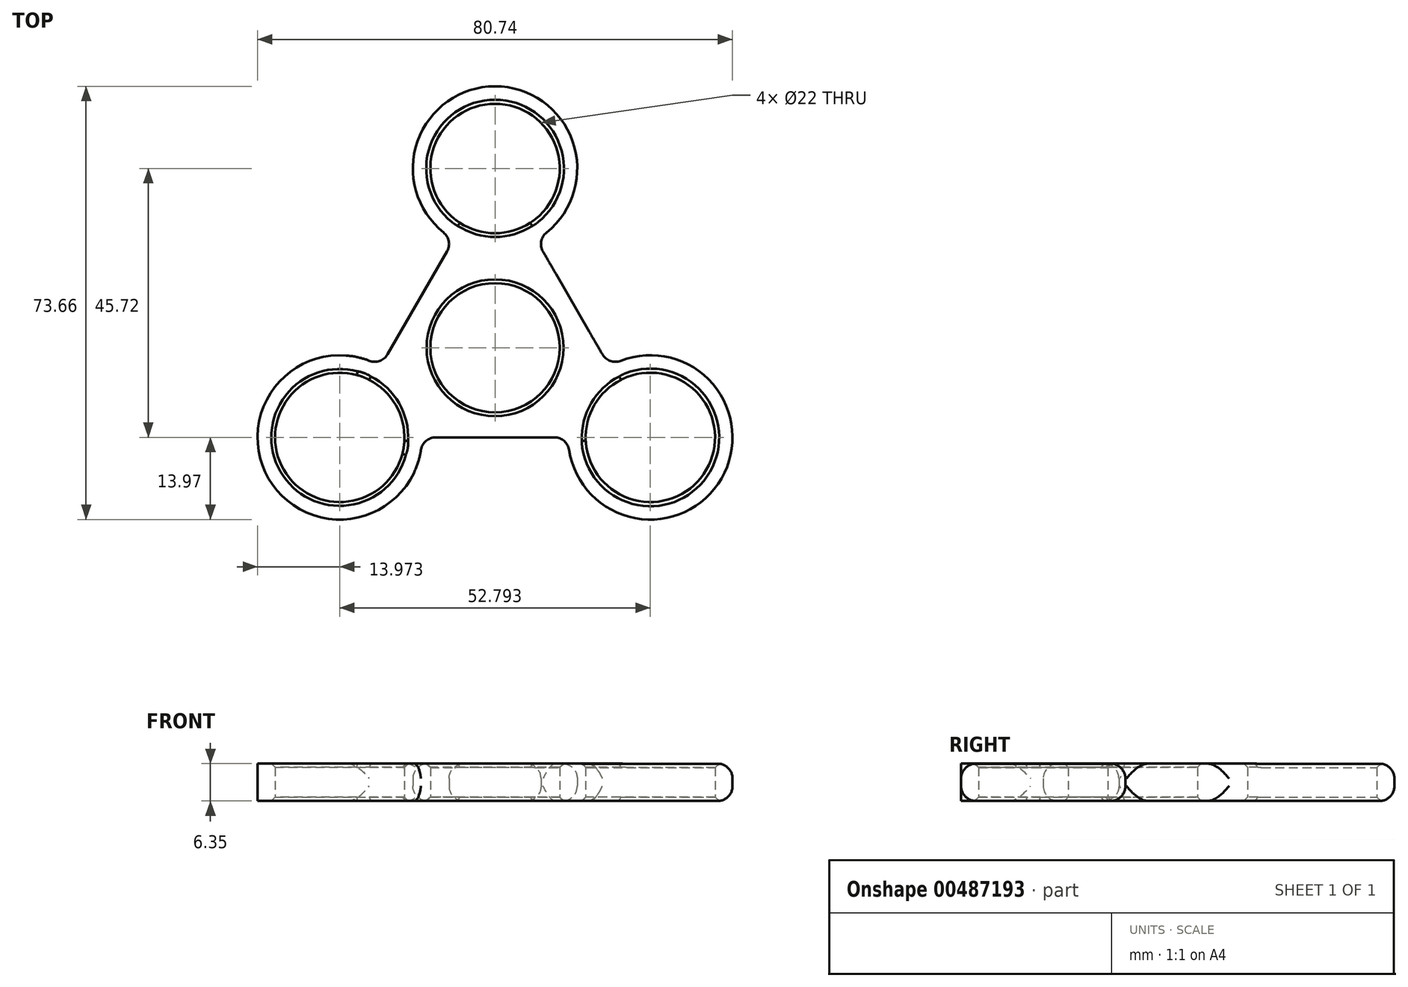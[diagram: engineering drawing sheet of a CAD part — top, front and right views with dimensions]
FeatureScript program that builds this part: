
annotation { "Feature Type Name" : "Feature", "Feature Type Description" : "" }
export const myFeature = defineFeature(function(context is Context, id is Id, definition is map)
    precondition{}
    {
        {
            var Q0;
            Q0=qCreatedBy(makeId("Top.planeOp"),FACE);
            var sketch = newSketch(context, id + "F0", { "sketchPlane" : qUnion([Q0])});
            skCircle(sketch, "E0", {"center": v(0, 0) * mm, "radius": 44.45 * mm});
            skCircle(sketch, "E1", {"center": v(0, 0) * mm, "radius": 11 * mm});
            skCircle(sketch, "E2", {"center": v(0, 30.48) * mm, "radius": 11 * mm});
            skCircle(sketch, "E3.1.0", {"center": v(-26.4, -15.24) * mm, "radius": 11 * mm});
            skCircle(sketch, "E3.2.0", {"center": v(26.4, -15.24) * mm, "radius": 11 * mm});
            skCircle(sketch, "E4", {"center": v(0, 30.48) * mm, "radius": 13.97 * mm});
            skCircle(sketch, "E5", {"center": v(-26.4, -15.24) * mm, "radius": 13.97 * mm});
            skCircle(sketch, "E6", {"center": v(26.4, -15.24) * mm, "radius": 13.97 * mm});
            skCircle(sketch, "E7", {"center": v(0, 0) * mm, "radius": 13.97 * mm});
            skCircle(sketch, "E8.cCircle", {"center": v(0, 0) * mm, "radius": 30.48 * mm, "construction": true});
            skLineSegment(sketch, "E8.0", {"start": v(6.99, 18.38) * mm, "end": v(19.41, -3.14) * mm});
            skLineSegment(sketch, "E8.1", {"start": v(12.43, -15.24) * mm, "end": v(-12.43, -15.24) * mm});
            skLineSegment(sketch, "E8.2", {"start": v(-19.41, -3.14) * mm, "end": v(-6.98, 18.38) * mm});
            skSolve(sketch);
        }
        {
            var Q0;
            Q0=makeQuery(id+"F0.imprint","IMPRINT",FACE,{"disambiguationData":[TD([[makeQuery(id+"F0.imprint","IMPRINT",EDGE,{"derivedFrom":sQuery(id+"F0.wireOp",EDGE,"E2")}),-1.0]])]});
            var Q1;
            Q1=makeQuery(id+"F0.imprint","IMPRINT",FACE,{"disambiguationData":[TD([[makeQuery(id+"F0.imprint","IMPRINT",EDGE,{"derivedFrom":sQuery(id+"F0.wireOp",EDGE,"E3.2.0")}),-1.0]])]});
            var Q2;
            Q2=makeQuery(id+"F0.imprint","IMPRINT",FACE,{"disambiguationData":[TD([[makeQuery(id+"F0.imprint","IMPRINT",EDGE,{"derivedFrom":sQuery(id+"F0.wireOp",EDGE,"E3.1.0")}),-1.0]])]});
            var Q3;
            Q3=makeQuery(id+"F0.imprint","IMPRINT",FACE,{"disambiguationData":[TD([[makeQuery(id+"F0.imprint","IMPRINT",EDGE,{"derivedFrom":sQuery(id+"F0.wireOp",EDGE,"E7")}),-1.0]])]});
            var Q4;
            Q4=makeQuery(id+"F0.imprint","IMPRINT",FACE,{"disambiguationData":[TD([[makeQuery(id+"F0.imprint","IMPRINT",EDGE,{"derivedFrom":sQuery(id+"F0.wireOp",EDGE,"E1")}),-1.0]])]});
            extrude(context, id + "F1", {"entities" : qUnion([Q0, Q1, Q2, Q3, Q4]), "depth" : 6.35 * mm});
        }
        {
            var Q0;
            Q0=makeQuery(id+"F1.opExtrude","SWEPT_FACE",FACE,{"disambiguationData":[OSD([sQuery(id+"F0.wireOp",EDGE,"E8.2")])]});
            var Q1;
            Q1=makeQuery(id+"F1.opExtrude","SWEPT_FACE",FACE,{"disambiguationData":[OSD([sQuery(id+"F0.wireOp",EDGE,"E4")])]});
            fillet(context, id + "F2", {"entities" : qUnion([Q0, Q1]), "radius" : 2.54 * mm, "tangentPropagation" : true, "allowEdgeOverflow" : false});
        }
        {
            var Q0;
            Q0=makeQuery(id+"F1.opExtrude","SWEPT_FACE",FACE,{"disambiguationData":[OSD([sQuery(id+"F0.wireOp",EDGE,"E8.1")])]});
            var Q1;
            Q1=makeQuery(id+"F1.opExtrude","SWEPT_FACE",FACE,{"disambiguationData":[OSD([sQuery(id+"F0.wireOp",EDGE,"E6")])]});
            fillet(context, id + "F3", {"entities" : qUnion([Q0, Q1]), "radius" : 2.54 * mm, "tangentPropagation" : true, "allowEdgeOverflow" : false});
        }
        {
            var Q0;
            Q0=makeQuery(id+"F1.opExtrude","CAP_EDGE",EDGE,{"disambiguationData":[OSD([sQuery(id+"F0.wireOp",EDGE,"E1")])],"isStart":false});
            var Q1;
            Q1=makeQuery(id+"F1.opExtrude","CAP_EDGE",EDGE,{"disambiguationData":[OSD([sQuery(id+"F0.wireOp",EDGE,"E1")])],"isStart":true});
            var Q2;
            Q2=makeQuery(id+"F1.opExtrude","CAP_EDGE",EDGE,{"disambiguationData":[OSD([sQuery(id+"F0.wireOp",EDGE,"E2")])],"isStart":false});
            var Q3;
            Q3=makeQuery(id+"F1.opExtrude","CAP_EDGE",EDGE,{"disambiguationData":[OSD([sQuery(id+"F0.wireOp",EDGE,"E3.2.0")])],"isStart":false});
            var Q4;
            Q4=makeQuery(id+"F1.opExtrude","CAP_EDGE",EDGE,{"disambiguationData":[OSD([sQuery(id+"F0.wireOp",EDGE,"E3.1.0")])],"isStart":false});
            var Q5;
            Q5=makeQuery(id+"F1.opExtrude","CAP_EDGE",EDGE,{"disambiguationData":[OSD([sQuery(id+"F0.wireOp",EDGE,"E2")])],"isStart":true});
            var Q6;
            Q6=makeQuery(id+"F1.opExtrude","CAP_EDGE",EDGE,{"disambiguationData":[OSD([sQuery(id+"F0.wireOp",EDGE,"E3.2.0")])],"isStart":true});
            var Q7;
            Q7=makeQuery(id+"F1.opExtrude","CAP_EDGE",EDGE,{"disambiguationData":[OSD([sQuery(id+"F0.wireOp",EDGE,"E3.1.0")])],"isStart":true});
            chamfer(context, id + "F4", {"entities" : qUnion([Q0, Q1, Q2, Q3, Q4, Q5, Q6, Q7]), "width" : 0.64 * mm, "tangentPropagation" : true});
        }
    });
